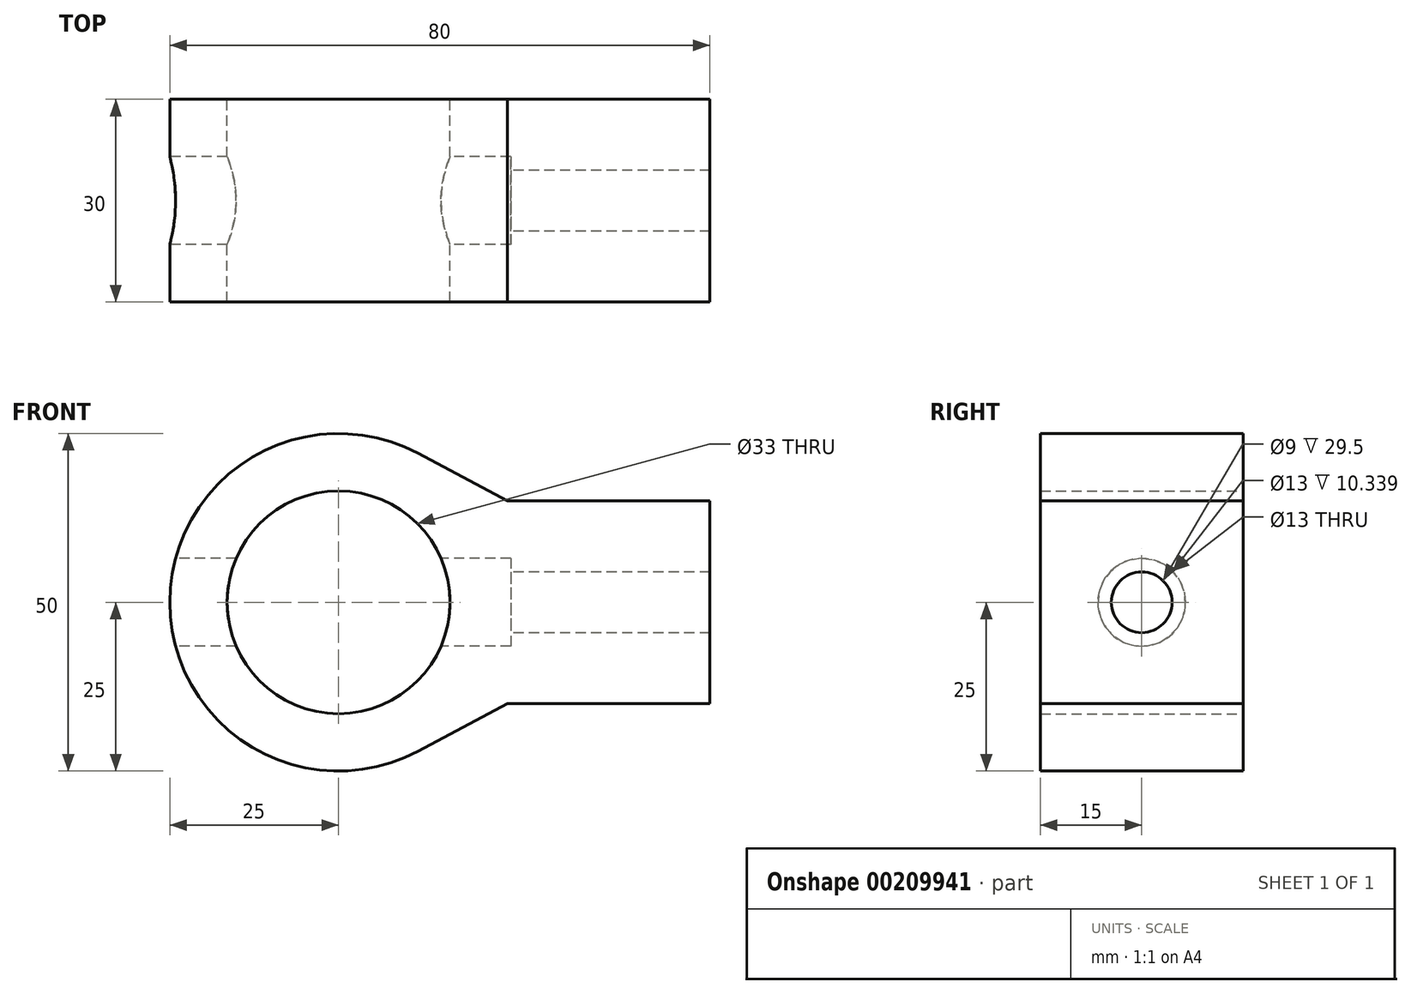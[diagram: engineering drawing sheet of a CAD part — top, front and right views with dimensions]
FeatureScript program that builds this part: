
annotation { "Feature Type Name" : "Feature", "Feature Type Description" : "" }
export const myFeature = defineFeature(function(context is Context, id is Id, definition is map)
    precondition{}
    {
        {
            var Q0;
            Q0=qCreatedBy(makeId("Front.planeOp"),FACE);
            var sketch = newSketch(context, id + "F0", { "sketchPlane" : qUnion([Q0])});
            skLineSegment(sketch, "E0.bottom", {"start": v(15, -15) * mm, "end": v(-15, -15) * mm});
            skLineSegment(sketch, "E0.top", {"start": v(15, 15) * mm, "end": v(-15, 15) * mm});
            skLineSegment(sketch, "E0.left", {"start": v(15, -15) * mm, "end": v(15, 15) * mm});
            skLineSegment(sketch, "E0.right", {"start": v(-15, -15) * mm, "end": v(-15, 15) * mm});
            skPoint(sketch, "E0.middle", {"position": v(0, 0) * mm});
            skLineSegment(sketch, "E1", {"start": v(0, 0) * mm, "end": v(-15, 0) * mm});
            skLineSegment(sketch, "E2", {"start": v(-15, 0) * mm, "end": v(-40, 0) * mm});
            skPoint(sketch, "E3", {"position": v(-40, 0) * mm});
            skPoint(sketch, "E4", {"position": v(-15, 0) * mm});
            skPoint(sketch, "E5", {"position": v(-15, 15) * mm});
            skPoint(sketch, "E6", {"position": v(-15, -15) * mm});
            skCircle(sketch, "E7", {"center": v(-40, 0) * mm, "radius": 25 * mm});
            skCircle(sketch, "E8", {"center": v(-40, 0) * mm, "radius": 16.5 * mm});
            skPoint(sketch, "E9", {"position": v(-23.5, 0) * mm});
            skPoint(sketch, "E10", {"position": v(-56.5, 0) * mm});
            skLineSegment(sketch, "E11", {"start": v(-15, 15) * mm, "end": v(-28.24, 22.06) * mm});
            skLineSegment(sketch, "E12", {"start": v(-15, -15) * mm, "end": v(-28.24, -22.06) * mm});
            skSolve(sketch);
        }
        {
            var Q0;
            Q0=makeQuery(id+"F0.imprint","IMPRINT",FACE,{"disambiguationData":[TD([[makeQuery(id+"F0.imprint","IMPRINT",EDGE,{"derivedFrom":sQuery(id+"F0.wireOp",EDGE,"E8")}),-1.0]])]});
            var Q1;
            {var subQ0=sQuery(id+"F0.wireOp",EDGE,"E11");Q1=makeQuery(id+"F0.imprint","IMPRINT",FACE,{"disambiguationData":[TD([[makeQuery(id+"F0.imprint","IMPRINT",EDGE,{"derivedFrom":subQ0}),1.0]])]});}
            var Q2;
            {var subQ0=sQuery(id+"F0.wireOp",EDGE,"E12");Q2=makeQuery(id+"F0.imprint","IMPRINT",FACE,{"disambiguationData":[TD([[makeQuery(id+"F0.imprint","IMPRINT",EDGE,{"derivedFrom":subQ0}),-1.0]])]});}
            var Q3;
            {var subQ1=sQuery(id+"F0.wireOp",EDGE,"E0.bottom");Q3=makeQuery(id+"F0.imprint","IMPRINT",FACE,{"disambiguationData":[TD([[makeQuery(id+"F0.imprint","IMPRINT",EDGE,{"derivedFrom":subQ1}),-1.0]])]});}
            extrude(context, id + "F1", {"entities" : qUnion([Q0, Q1, Q2, Q3]), "depth" : 30 * mm});
        }
        {
            var Q0;
            Q0=makeQuery(id+"F1.opExtrude","SWEPT_FACE",FACE,{"disambiguationData":[OSD([sQuery(id+"F0.wireOp",EDGE,"E0.left")])]});
            var sketch = newSketch(context, id + "F2", { "sketchPlane" : qUnion([Q0])});
            skPoint(sketch, "E13", {"position": v(-30, 0) * mm});
            skLineSegment(sketch, "E14", {"start": v(-30, 0) * mm, "end": v(0, 0) * mm});
            skPoint(sketch, "E15", {"position": v(-15, 0) * mm});
            skPoint(sketch, "E16", {"position": v(0, 0) * mm});
            skSolve(sketch);
        }
        {
            var Q0;
            {var subQ0=sQuery(id+"F2.wireOp",EDGE,"E14");Q0=makeQuery(id+"F2.imprint","IMPRINT",FACE,{"disambiguationData":[TD([[makeQuery(id+"F2.imprint","IMPRINT",EDGE,{"derivedFrom":subQ0}),1.0]])]});}
            cPlane(context, id + "F3", {"entities" : qUnion([Q0]), "cplaneType" : CPlaneType.OFFSET, "offset" : 40 * mm, "oppositeDirection" : true, "width" : 150 * mm, "height" : 150 * mm});
        }
        {
            var Q0;
            Q0=qCreatedBy(id+"F3.planeOp",FACE);
            var sketch = newSketch(context, id + "F4", { "sketchPlane" : qUnion([Q0])});
            skLineSegment(sketch, "E17", {"start": v(0, 0) * mm, "end": v(-30, 0) * mm});
            skPoint(sketch, "E18", {"position": v(-15, 0) * mm});
            skSolve(sketch);
        }
        {
            var Q0;
            Q0=sQuery(id+"F4.wireOp",VERTEX,"E18");
            var Q1;
            Q1=makeQuery(id+"F1.opExtrude","SWEPT_BODY",BODY,{"disambiguationData":[OSD([sQuery(id+"F0.wireOp",EDGE,"E0.bottom"),sQuery(id+"F0.wireOp",EDGE,"E0.top"),sQuery(id+"F0.wireOp",EDGE,"E0.left"),sQuery(id+"F0.wireOp",EDGE,"E7"),sQuery(id+"F0.wireOp",EDGE,"E8"),sQuery(id+"F0.wireOp",EDGE,"E11"),sQuery(id+"F0.wireOp",EDGE,"E12")])]});
            hole(context, id + "F5", {"style" : HoleStyle.C_BORE, "endStyle" : HoleEndStyle.THROUGH, "oppositeDirection" : true, "holeDiameter" : 9 * mm, "cBoreDiameter" : 13 * mm, "cBoreDepth" : 9 * mm, "locations" : qUnion([Q0]), "scope" : qUnion([Q1]), "isTappedThrough" : true});
        }
        {
            var Q0;
            {var subQ0=sQuery(id+"F2.wireOp",EDGE,"E14");Q0=makeQuery(id+"F2.imprint","IMPRINT",FACE,{"disambiguationData":[TD([[makeQuery(id+"F2.imprint","IMPRINT",EDGE,{"derivedFrom":subQ0}),1.0]])]});}
            cPlane(context, id + "F6", {"entities" : qUnion([Q0]), "cplaneType" : CPlaneType.OFFSET, "offset" : 80 * mm, "oppositeDirection" : true, "width" : 150 * mm, "height" : 150 * mm});
        }
        {
            var Q0;
            Q0=qCreatedBy(id+"F6.planeOp",FACE);
            var sketch = newSketch(context, id + "F7", { "sketchPlane" : qUnion([Q0])});
            skLineSegment(sketch, "E19", {"start": v(-30, 0) * mm, "end": v(0, 0) * mm});
            skPoint(sketch, "E20", {"position": v(-15, 0) * mm});
            skSolve(sketch);
        }
        {
            var Q0;
            Q0=sQuery(id+"F7.wireOp",VERTEX,"E20");
            var Q1;
            Q1=makeQuery(id+"F1.opExtrude","SWEPT_BODY",BODY,{"disambiguationData":[OSD([sQuery(id+"F0.wireOp",EDGE,"E0.bottom"),sQuery(id+"F0.wireOp",EDGE,"E0.top"),sQuery(id+"F0.wireOp",EDGE,"E0.left"),sQuery(id+"F0.wireOp",EDGE,"E7"),sQuery(id+"F0.wireOp",EDGE,"E8"),sQuery(id+"F0.wireOp",EDGE,"E11"),sQuery(id+"F0.wireOp",EDGE,"E12")])]});
            hole(context, id + "F8", {"style" : HoleStyle.SIMPLE, "endStyle" : HoleEndStyle.BLIND, "oppositeDirection" : true, "holeDiameter" : 13 * mm, "holeDepth" : 20 * mm, "locations" : qUnion([Q0]), "scope" : qUnion([Q1])});
        }
    });
